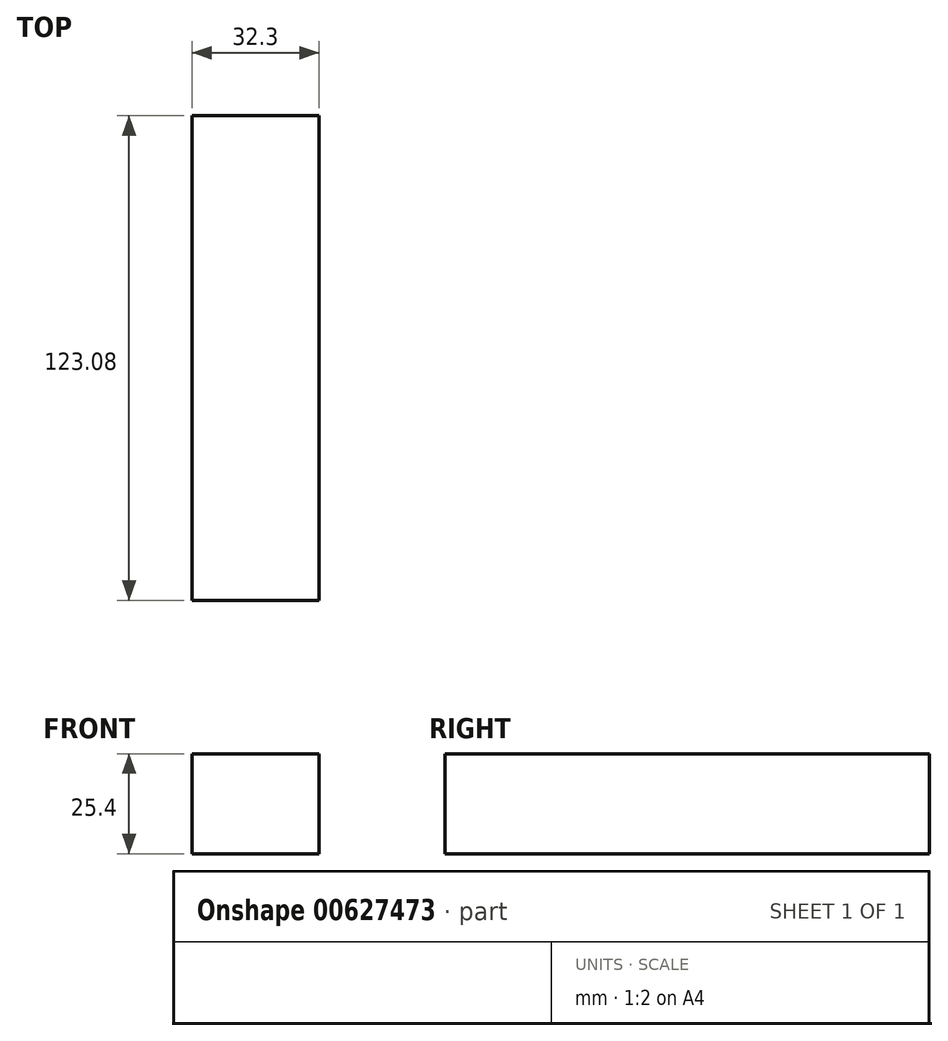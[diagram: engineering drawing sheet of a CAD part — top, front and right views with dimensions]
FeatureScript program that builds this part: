
annotation { "Feature Type Name" : "Feature", "Feature Type Description" : "" }
export const myFeature = defineFeature(function(context is Context, id is Id, definition is map)
    precondition{}
    {
        {
            var Q0;
            Q0=qCreatedBy(makeId("Top.planeOp"),FACE);
            var sketch = newSketch(context, id + "F0", { "sketchPlane" : qUnion([Q0])});
            skLineSegment(sketch, "E0.bottom", {"start": v(0, -61.37) * mm, "end": v(-32.3, -61.37) * mm});
            skLineSegment(sketch, "E0.top", {"start": v(0, 61.71) * mm, "end": v(-32.3, 61.71) * mm});
            skLineSegment(sketch, "E0.left", {"start": v(0, -61.37) * mm, "end": v(0, 61.71) * mm});
            skLineSegment(sketch, "E0.right", {"start": v(-32.3, -61.37) * mm, "end": v(-32.3, 61.71) * mm});
            skSolve(sketch);
        }
        {
            var Q0;
            Q0=makeQuery(id+"F0.imprint","IMPRINT",FACE,{"disambiguationData":[TD([[makeQuery(id+"F0.imprint","IMPRINT",EDGE,{"derivedFrom":sQuery(id+"F0.wireOp",EDGE,"E0.bottom")}),-1.0]])]});
            extrude(context, id + "F1", {"entities" : qUnion([Q0]), "depth" : 25.4 * mm, "offsetDistance" : 25.4 * mm});
        }
    });
